# Revit family: WAGNER_Плата_сетевая_TITANUS_NU-5-D
name_source: partatom
category: Оборудование
revit_build: Autodesk Revit 2017 (Build: 20170118_1100(x64)
units: mm (PartAtom-declared; Revit-internal decimal feet)

## family parameters
Всегда вертикально = Да
Заголовок OmniClass = Alarm Panels
На основе рабочей плоскости = Нет
Номер OmniClass = 23.85.30.21.11.14
Общий = Да
При загрузке вырезать с полостями = Нет
Размер круглого соединителя = Использовать диаметр
Тип детали = Вставляется
Точка расчета площади = Нет

## types (1)
- Typ NU-5-D
    ADSK_URL документации изделия = https://ru.wagnergroup.com
    ADSK_URL страницы изделия = https://ru.wagnergroup.com
    ADSK_Версия Revit = Revit 2017
    ADSK_Версия семейства = Версия 1
    ADSK_Дата изменения = 19.07.20
    ADSK_Единица измерения = шт.
    ADSK_Завод-изготовитель = WAGNER
    ADSK_Код изделия = -
    ADSK_Марка = Typ NU-5-D
    ADSK_Материал = Стекло
    ADSK_Наименование = Плата сетевая TITANUS NU-5-D
    ADSK_Наименование краткое = Плата сетевая TITANUS NU-5-D
    ADSK_Размер_Высота = 0 мм
    ADSK_Размер_Длина = 0 мм
    ADSK_Размер_Ширина = 0 мм
    COBie Category = Fire alarm panels
    Masterformat Code = 28 46 23
    Masterformat Title = Fire Alarm Notification Appliances
    OmniClass Code = 23.85.30.21.11.14
    OmniClass Title = Alarm Panels
    UNSPSC Code = 46191505
    UNSPSC Title = Fire alarm systems
    URL = www.wagner-russia.com
    Uniclass Code = Pr_75_75_30_29
    Uniclass Title = Fire alarm panels
    WAGNER_Variation = 1
    WAGNER_Артикул = 09-20-6445
    WAGNER_Название = Плата сетевая TITANUS NU-5-D
    WAGNER_Тип = Typ NU-5-D
    bimon.ru = bimon.ru
    Изготовитель = WAGNER
    Описание = Плата сетевая TITANUS NU-5-D

## geometry (parser evidence)
native form markers: Blend x2
no freeform markers — native parametric forms only
